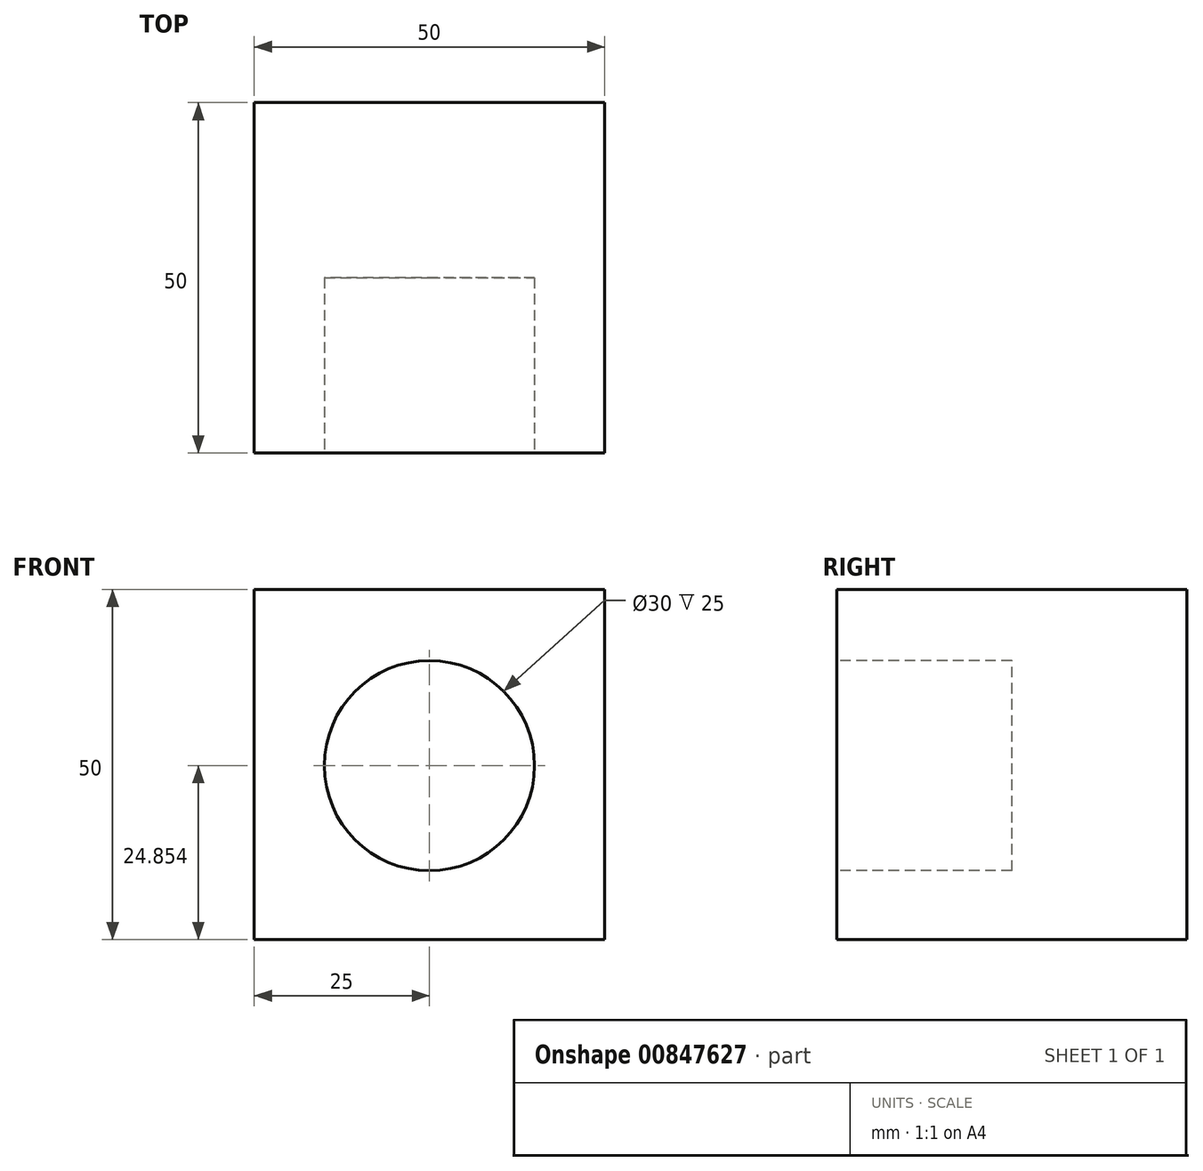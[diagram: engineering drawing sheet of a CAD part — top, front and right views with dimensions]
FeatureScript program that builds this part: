
annotation { "Feature Type Name" : "Feature", "Feature Type Description" : "" }
export const myFeature = defineFeature(function(context is Context, id is Id, definition is map)
    precondition{}
    {
        {
            var Q0;
            Q0=qCreatedBy(makeId("Top.planeOp"),FACE);
            var sketch = newSketch(context, id + "F0", { "sketchPlane" : qUnion([Q0])});
            skLineSegment(sketch, "E0.bottom", {"start": v(25, -25) * mm, "end": v(-25, -25) * mm});
            skLineSegment(sketch, "E0.top", {"start": v(25, 25) * mm, "end": v(-25, 25) * mm});
            skLineSegment(sketch, "E0.left", {"start": v(25, -25) * mm, "end": v(25, 25) * mm});
            skLineSegment(sketch, "E0.right", {"start": v(-25, -25) * mm, "end": v(-25, 25) * mm});
            skPoint(sketch, "E0.middle", {"position": v(0, 0) * mm});
            skSolve(sketch);
        }
        {
            var Q0;
            Q0 = qSketchRegion(id + "F0", true);
            extrude(context, id + "F1", {"entities" : qUnion([Q0]), "depth" : 50 * mm, "offsetDistance" : 25 * mm});
        }
        {
            var Q0;
            Q0=makeQuery(id+"F1.opExtrude","SWEPT_FACE",FACE,{"disambiguationData":[OSD([sQuery(id+"F0.wireOp",EDGE,"E0.bottom")])]});
            var sketch = newSketch(context, id + "F2", { "sketchPlane" : qUnion([Q0])});
            skCircle(sketch, "E1", {"center": v(0, 24.85) * mm, "radius": 15 * mm});
            skSolve(sketch);
        }
        {
            var Q0;
            Q0 = qSketchRegion(id + "F2", true);
            extrude(context, id + "F3", {"entities" : qUnion([Q0]), "operationType" : NewBodyOperationType.REMOVE, "oppositeDirection" : true, "depth" : 25 * mm, "offsetDistance" : 25 * mm});
        }
    });
